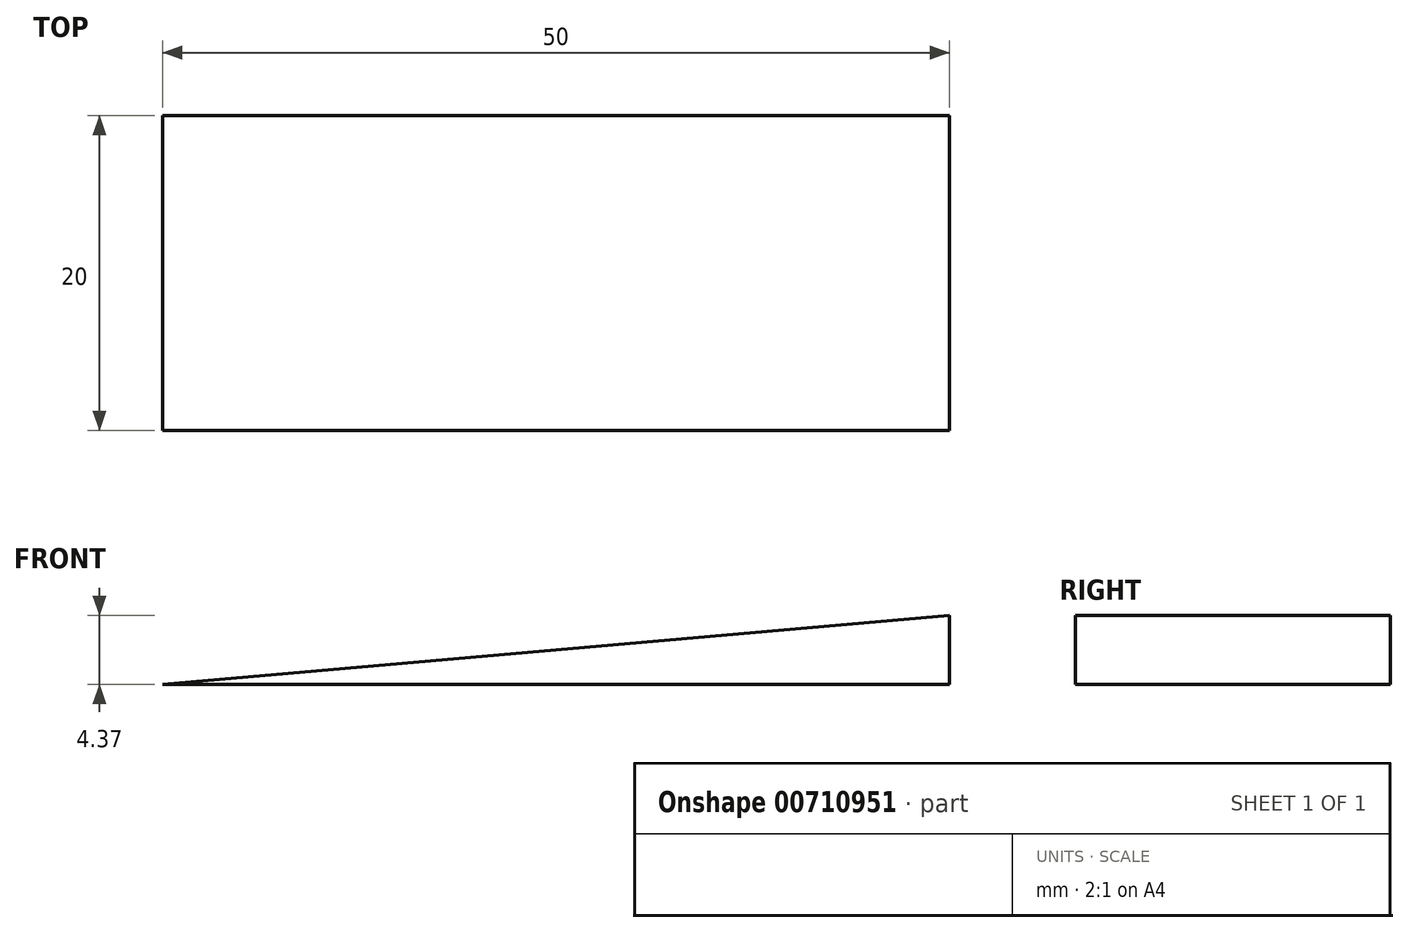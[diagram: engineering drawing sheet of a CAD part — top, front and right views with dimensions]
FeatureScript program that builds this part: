
annotation { "Feature Type Name" : "Feature", "Feature Type Description" : "" }
export const myFeature = defineFeature(function(context is Context, id is Id, definition is map)
    precondition{}
    {
        {
            var Q0;
            Q0=qCreatedBy(makeId("Top.planeOp"),FACE);
            var sketch = newSketch(context, id + "F0", { "sketchPlane" : qUnion([Q0])});
            skLineSegment(sketch, "E0.bottom", {"start": v(25, -10) * mm, "end": v(-25, -10) * mm});
            skLineSegment(sketch, "E0.top", {"start": v(25, 10) * mm, "end": v(-25, 10) * mm});
            skLineSegment(sketch, "E0.left", {"start": v(25, -10) * mm, "end": v(25, 10) * mm});
            skLineSegment(sketch, "E0.right", {"start": v(-25, -10) * mm, "end": v(-25, 10) * mm});
            skPoint(sketch, "E0.middle", {"position": v(0, 0) * mm});
            skSolve(sketch);
        }
        {
            var Q0;
            Q0=makeQuery(id+"F0.imprint","IMPRINT",FACE,{"disambiguationData":[TD([[makeQuery(id+"F0.imprint","IMPRINT",EDGE,{"derivedFrom":sQuery(id+"F0.wireOp",EDGE,"E0.bottom")}),-1.0]])]});
            extrude(context, id + "F1", {"entities" : qUnion([Q0]), "depth" : 5 * mm, "offsetDistance" : 25 * mm});
        }
        {
            var Q0;
            Q0=makeQuery(id+"F1.opExtrude","CAP_EDGE",EDGE,{"disambiguationData":[OSD([sQuery(id+"F0.wireOp",EDGE,"E0.right")])],"isStart":false});
            chamfer(context, id + "F2", {"entities" : qUnion([Q0]), "chamferType" : ChamferType.OFFSET_ANGLE, "width" : 5 * mm, "oppositeDirection" : false, "angle" : 85 * degree, "tangentPropagation" : true});
        }
    });
